# Revit family: REIDLifting_TDAVIT_TDT_GearedTrolley
name_source: partatom
category: Specialty Equipment
units: mm (PartAtom-declared; Revit-internal decimal feet)

## family parameters
Always vertical = Yes
Cut with Voids When Loaded = No
OmniClass Number = 23.50.05.14
OmniClass Title = Lifts
Part Type = Normal
Room Calculation Point = No
Round Connector Dimension = Use Diameter
Shared = No
Work Plane-Based = No

## types (12) — shared parameters
Assembly Code = D1010300
AssetType = Fixed
BIMObjectName = REIDLifting_TDAVIT_TDT_GearedTrolley
BridgeMountSocketSBMA0500 = BridgeMountSocket : SBMA0500
BridgeMountSocketSBMG0500 = BridgeMountSocket : SBMG0500
BridgeMountSocketSBMS0500 = BridgeMountSocket : SBMS0500
ClassificationName = Uniclass2015
ClassificationValue = TE_30_30_10
Color = Grey & Blue
Description = Our TDAVIT - TDT is lightweight, portable and has been designed to meet customer needs where the lifting and moving of equipment in tight spaces is a challenge.
DocumentationCertificates = https://www.bimstore.co
DocumentationInstallationGuide = https://www.bimstore.co
DocumentationLiterature = https://www.bimstore.co
DocumentationMaintenance = https://www.bimstore.co
DocumentationTechnical = https://www.bimstore.co
DurationUnit = Years
Finish = Painted Steel
IfcExportAs = IfcBuildingElementProxy
IfcExportType = IfcBuildingElementProxy
Keynote = N
Manufacturer = REID Lifting
ManufacturerName = REID Lifting
Material = Steel
Model = TDAVIT TDT - Geared Trolley
ModelReference = TDAVIT TDT - Geared Trolley
NBSDescription = Construction lifts
NBSObjectName = REID Lifting - Construction lifts
ProductionYear = 2023
SideMountSocketSSMA0500 = SideMountSocket : SSMA0500
SideMountSocketSSMG0500V2 = SideMountSocket : SSMG0500V2
SideMountSocketSSMG1000 = SideMountSocket : SSMG1000
SideMountSocketSSMS0500V2 = SideMountSocket : SSMS0500V2
SideMountSocketSSMS1000 = SideMountSocket : SSMS1000
SocketPedestalsSP0500 = SocketPedestals : SP0500
SocketPedestalsSP0800 = SocketPedestals : SP0800
SocketPedestalsSP1100 = SocketPedestals : SP1100
TopMountSocketSTMA0500 = TopMountSocket : STMA0500
TopMountSocketSTMG0500V2 = TopMountSocket : STMG0500V2
TopMountSocketSTMG1000 = TopMountSocket : STMG1000
TopMountSocketSTMS0500V2 = TopMountSocket : STMS0500V2
TopMountSocketSTMS1000 = TopMountSocket : STMS1000
TypeName = TDAVIT TDT - Geared Trolley
URL = https://uk.reidlifting.com
WarrantyDurationLabor = 0
WarrantyDurationParts = 0
WarrantyDurationUnit = Years
_BSBibleVersion = 17
_CurrentRevision = 1
_DistributedBy = https://www.bimstore.co
_ObjectUserGuide = https://www.bimstore.co
zero-valued in all types: Cost, ExpectedLife, NominalDepth, NominalHeight, NominalLength, _BimSpecGuid

## per-type parameters (varying)
| type | TopBeamLength |
| TDTA51200 | 1369 mm  [stored 4.49147 ft] |
| TDTA32000 | 2147 mm  [stored 7.04396 ft] |
| TDTA31700 | 1865 mm  [stored 6.11877 ft] |
| TDTA31500 | 1647 mm  [stored 5.40354 ft] |
| TDTA31200 | 1369 mm  [stored 4.49147 ft] |
| TDTA42000 | 2147 mm  [stored 7.04396 ft] |
| TDTA41700 | 1865 mm  [stored 6.11877 ft] |
| TDTA41500 | 1647 mm  [stored 5.40354 ft] |
| TDTA41200 | 1369 mm  [stored 4.49147 ft] |
| TDTA52000 | 2147 mm  [stored 7.04396 ft] |
| TDTA51700 | 1865 mm  [stored 6.11877 ft] |
| TDTA51500 | 1647 mm  [stored 5.40354 ft] |

note: column(s) folded — value = type name in every type: ModelNumber, Type Comments

note: [stored X ft] marks values corroborated as IEEE doubles in the binary element streams (Revit-internal decimal feet)

## geometry (parser evidence)
native form markers: Sweep x24
no freeform markers — native parametric forms only
